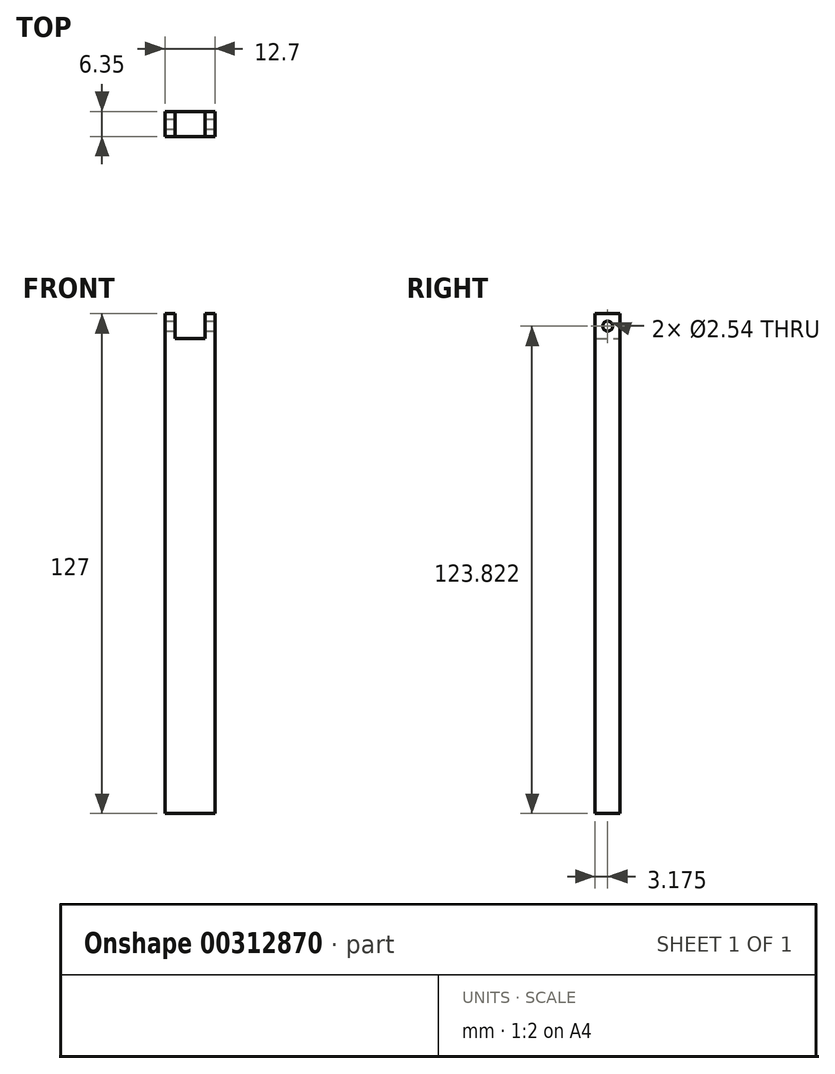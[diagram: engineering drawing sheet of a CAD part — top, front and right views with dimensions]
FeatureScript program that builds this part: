
annotation { "Feature Type Name" : "Feature", "Feature Type Description" : "" }
export const myFeature = defineFeature(function(context is Context, id is Id, definition is map)
    precondition{}
    {
        {
            var Q0;
            Q0=qCreatedBy(makeId("Front.planeOp"),FACE);
            var sketch = newSketch(context, id + "F0", { "sketchPlane" : qUnion([Q0])});
            skLineSegment(sketch, "E0", {"start": v(-7.65, 100) * mm, "end": v(-7.65, -27) * mm});
            skLineSegment(sketch, "E1", {"start": v(-7.65, -27) * mm, "end": v(5.05, -27) * mm});
            skLineSegment(sketch, "E2", {"start": v(5.05, -27) * mm, "end": v(5.05, 100) * mm});
            skLineSegment(sketch, "E3", {"start": v(5.05, 100) * mm, "end": v(-7.65, 100) * mm});
            skSolve(sketch);
        }
        {
            var Q0;
            Q0 = qSketchRegion(id + "F0", true);
            extrude(context, id + "F1", {"entities" : qUnion([Q0]), "depth" : 6.35 * mm});
        }
        {
            var Q0;
            Q0=qCreatedBy(makeId("Front.planeOp"),FACE);
            var sketch = newSketch(context, id + "F2", { "sketchPlane" : qUnion([Q0])});
            skLineSegment(sketch, "E4.0.0", {"start": v(5.05, -27) * mm, "end": v(5.05, 100) * mm});
            skLineSegment(sketch, "E4.0.1", {"start": v(5.05, 100) * mm, "end": v(-7.65, 100) * mm});
            skLineSegment(sketch, "E4.0.2", {"start": v(-7.65, 100) * mm, "end": v(-7.65, -27) * mm});
            skLineSegment(sketch, "E4.0.3", {"start": v(-7.65, -27) * mm, "end": v(5.05, -27) * mm});
            skLineSegment(sketch, "E5.bottom", {"start": v(2.51, 93.66) * mm, "end": v(-5.1, 93.66) * mm});
            skPoint(sketch, "E5.middle", {"position": v(-1.3, 100) * mm});
            skLineSegment(sketch, "E6", {"start": v(-5.1, 93.66) * mm, "end": v(-5.1, 100) * mm});
            skLineSegment(sketch, "E7", {"start": v(2.51, 93.66) * mm, "end": v(2.51, 100) * mm});
            skSolve(sketch);
        }
        {
            var Q0;
            Q0=makeQuery(id+"F2.imprint","IMPRINT",FACE,{"disambiguationData":[TD([[makeQuery(id+"F2.imprint","IMPRINT",EDGE,{"derivedFrom":sQuery(id+"F2.wireOp",EDGE,"E5.bottom")}),-1.0]])]});
            extrude(context, id + "F3", {"entities" : qUnion([Q0]), "operationType" : NewBodyOperationType.REMOVE, "endBound" : BoundingType.THROUGH_ALL, "depth" : 25.4 * mm});
        }
        {
            var Q0;
            Q0=makeQuery(id+"F3.boolean.opBoolean","COPY",FACE,{"derivedFrom":makeQuery(id+"F3.opExtrude","SWEPT_FACE",FACE,{"disambiguationData":[OSD([sQuery(id+"F2.wireOp",EDGE,"E6")])]})});
            var sketch = newSketch(context, id + "F4", { "sketchPlane" : qUnion([Q0])});
            skCircle(sketch, "E8", {"center": v(-3.17, 96.83) * mm, "radius": 1.27 * mm});
            skPoint(sketch, "E8.centerSnap0", {"position": v(-6.35, 96.83) * mm});
            skPoint(sketch, "E8.centerSnap1", {"position": v(-3.17, 100) * mm});
            skSolve(sketch);
        }
        {
            var Q0;
            Q0=makeQuery(id+"F4.imprint","IMPRINT",FACE,{"disambiguationData":[TD([[makeQuery(id+"F4.imprint","IMPRINT",EDGE,{"derivedFrom":sQuery(id+"F4.wireOp",EDGE,"E8")}),1.0]])]});
            extrude(context, id + "F5", {"entities" : qUnion([Q0]), "operationType" : NewBodyOperationType.REMOVE, "endBound" : BoundingType.SYMMETRIC, "oppositeDirection" : true, "depth" : 25.4 * mm});
        }
    });
